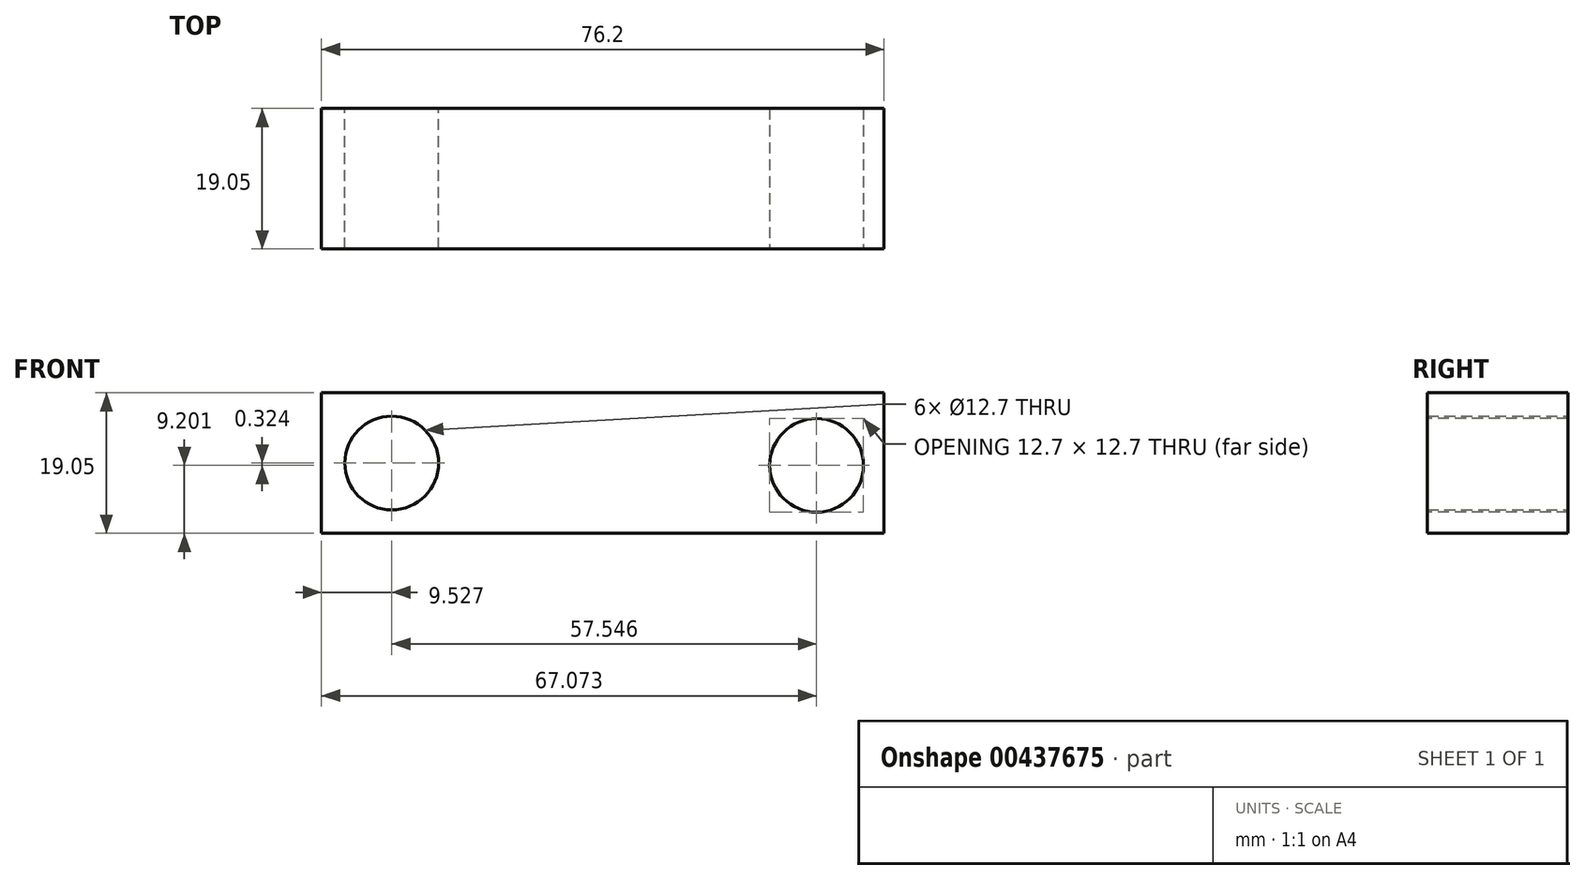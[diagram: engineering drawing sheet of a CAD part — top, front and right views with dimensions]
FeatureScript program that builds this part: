
annotation { "Feature Type Name" : "Feature", "Feature Type Description" : "" }
export const myFeature = defineFeature(function(context is Context, id is Id, definition is map)
    precondition{}
    {
        {
            var Q0;
            Q0=qCreatedBy(makeId("Top.planeOp"),FACE);
            var sketch = newSketch(context, id + "F0", { "sketchPlane" : qUnion([Q0])});
            skLineSegment(sketch, "E0.bottom", {"start": v(-28.48, 5.03) * mm, "end": v(47.72, 5.03) * mm});
            skLineSegment(sketch, "E0.top", {"start": v(-28.48, -14.02) * mm, "end": v(47.72, -14.02) * mm});
            skLineSegment(sketch, "E0.left", {"start": v(-28.48, 5.03) * mm, "end": v(-28.48, -14.02) * mm});
            skLineSegment(sketch, "E0.right", {"start": v(47.72, 5.03) * mm, "end": v(47.72, -14.02) * mm});
            skSolve(sketch);
        }
        {
            var Q0;
            Q0=makeQuery(id+"F0.imprint","IMPRINT",FACE,{"disambiguationData":[TD([[makeQuery(id+"F0.imprint","IMPRINT",EDGE,{"derivedFrom":sQuery(id+"F0.wireOp",EDGE,"E0.bottom")}),-1.0]])]});
            extrude(context, id + "F1", {"entities" : qUnion([Q0]), "depth" : 19.05 * mm});
        }
        {
            var Q0;
            Q0=makeQuery(id+"F1.opExtrude","SWEPT_FACE",FACE,{"disambiguationData":[OSD([sQuery(id+"F0.wireOp",EDGE,"E0.bottom")])]});
            var sketch = newSketch(context, id + "F2", { "sketchPlane" : qUnion([Q0])});
            skPoint(sketch, "E1", {"position": v(18.95, 9.53) * mm});
            skSolve(sketch);
        }
        {
            var Q0;
            Q0=sQuery(id+"F2.wireOp",VERTEX,"E1");
            var Q1;
            Q1=makeQuery(id+"F1.opExtrude","SWEPT_BODY",BODY,{"disambiguationData":[OSD([sQuery(id+"F0.wireOp",EDGE,"E0.bottom"),sQuery(id+"F0.wireOp",EDGE,"E0.top"),sQuery(id+"F0.wireOp",EDGE,"E0.left"),sQuery(id+"F0.wireOp",EDGE,"E0.right")])]});
            hole(context, id + "F3", {"style" : HoleStyle.SIMPLE, "endStyle" : HoleEndStyle.THROUGH, "holeDiameter" : 12.7 * mm, "isTappedThrough" : true, "tappedDepth" : 12.7 * mm, "tapClearance" : 3, "locations" : qUnion([Q0]), "scope" : qUnion([Q1])});
        }
        {
            var Q0;
            Q0=makeQuery(id+"F1.opExtrude","SWEPT_FACE",FACE,{"disambiguationData":[OSD([sQuery(id+"F0.wireOp",EDGE,"E0.top")])]});
            var sketch = newSketch(context, id + "F4", { "sketchPlane" : qUnion([Q0])});
            skCircle(sketch, "E2", {"center": v(38.6, 9.2) * mm, "radius": 6.35 * mm});
            skSolve(sketch);
        }
        {
            var Q0;
            Q0=makeQuery(id+"F4.imprint","IMPRINT",FACE,{"disambiguationData":[TD([[makeQuery(id+"F4.imprint","IMPRINT",EDGE,{"derivedFrom":sQuery(id+"F4.wireOp",EDGE,"E2")}),1.0]])]});
            var Q1;
            Q1=sQuery(id+"F4.wireOp",EDGE,"E2");
            extrude(context, id + "F5", {"entities" : qUnion([Q0]), "operationType" : NewBodyOperationType.REMOVE, "surfaceEntities" : qUnion([Q1]), "oppositeDirection" : true, "depth" : 51.05 * mm});
        }
    });
